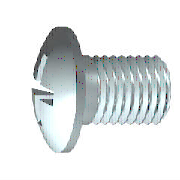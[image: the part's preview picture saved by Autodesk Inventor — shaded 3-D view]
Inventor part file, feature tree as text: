
AUTODESK INVENTOR PART (.ipt)
format: ipt  version: 2022 (Build 260153000, 153)  size: 258,048 bytes
history: native  units: mm (DEFAULTED — no unit token found)
features: other x3, extrude x1, plane x1
ambient origin geometry x7: Origin, YZ Plane, XZ Plane, X Axis, Y Axis, Z Axis, Center Point
bodies: Solid1 (feature_tree)
feature tree (5):
  other  "Базовый элемент"
  other  "IDS_WORKPLANE{1}"
  extrude  "Паз"  Depth=3.5052mm
  other  "Вырез"
  plane  "Work Plane3"
